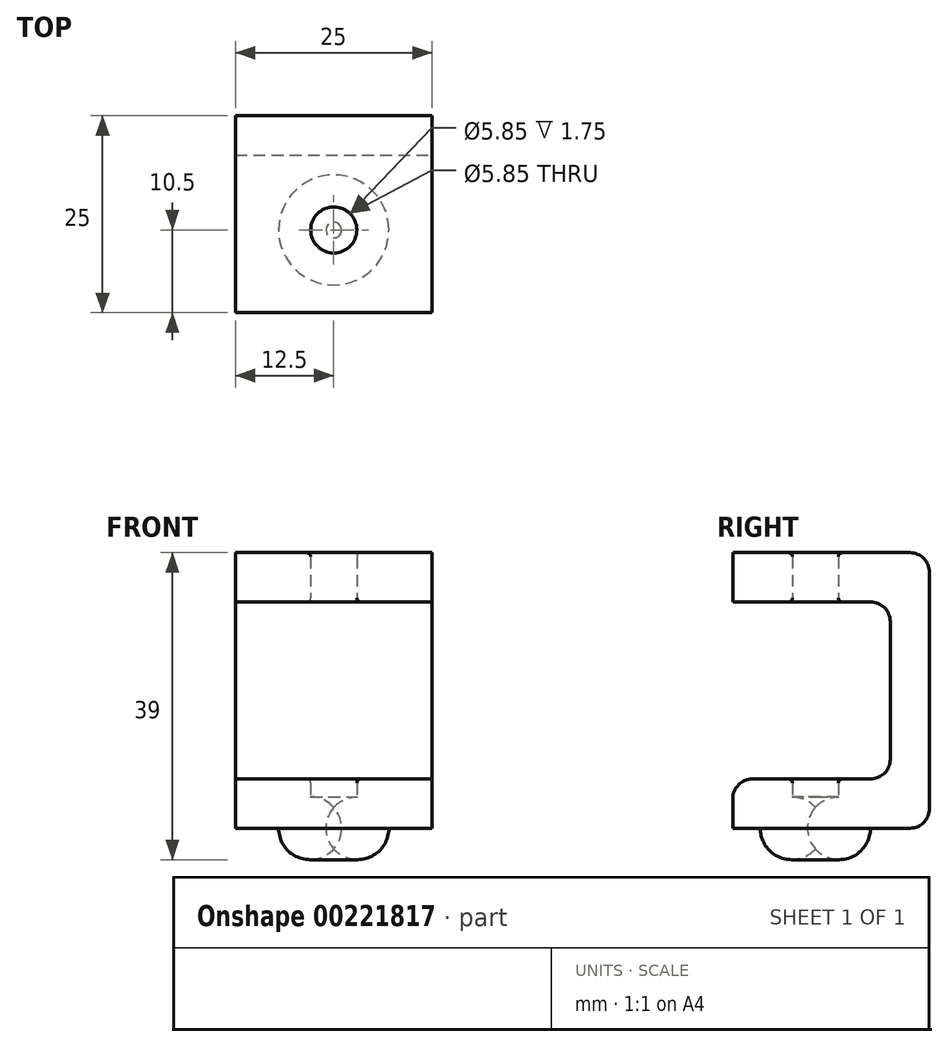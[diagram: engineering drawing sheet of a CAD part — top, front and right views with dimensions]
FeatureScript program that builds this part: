
annotation { "Feature Type Name" : "Feature", "Feature Type Description" : "" }
export const myFeature = defineFeature(function(context is Context, id is Id, definition is map)
    precondition{}
    {
        {
            var Q0;
            Q0=qCreatedBy(makeId("Top.planeOp"),FACE);
            var sketch = newSketch(context, id + "F0", { "sketchPlane" : qUnion([Q0])});
            skLineSegment(sketch, "E0.bottom", {"start": v(-12.5, -12.5) * mm, "end": v(12.5, -12.5) * mm});
            skLineSegment(sketch, "E0.top", {"start": v(-12.5, 12.5) * mm, "end": v(12.5, 12.5) * mm});
            skLineSegment(sketch, "E0.left", {"start": v(-12.5, -12.5) * mm, "end": v(-12.5, 12.5) * mm});
            skLineSegment(sketch, "E0.right", {"start": v(12.5, -12.5) * mm, "end": v(12.5, 12.5) * mm});
            skPoint(sketch, "E0.middle", {"position": v(0, 0) * mm});
            skLineSegment(sketch, "E1", {"start": v(0, -12.5) * mm, "end": v(0, 0) * mm, "construction": true});
            skCircle(sketch, "E2", {"center": v(0, -2) * mm, "radius": 2.93 * mm});
            skCircle(sketch, "E3", {"center": v(0, -2) * mm, "radius": 7 * mm});
            skSolve(sketch);
        }
        {
            var Q0;
            Q0=makeQuery(id+"F0.imprint","IMPRINT",FACE,{"disambiguationData":[TD([[makeQuery(id+"F0.imprint","IMPRINT",EDGE,{"derivedFrom":sQuery(id+"F0.wireOp",EDGE,"E0.bottom")}),1.0]])]});
            var Q1;
            Q1=makeQuery(id+"F0.imprint","IMPRINT",FACE,{"disambiguationData":[TD([[makeQuery(id+"F0.imprint","IMPRINT",EDGE,{"derivedFrom":sQuery(id+"F0.wireOp",EDGE,"E2")}),-1.0]])]});
            var Q2;
            Q2=makeQuery(id+"F0.imprint","IMPRINT",FACE,{"disambiguationData":[TD([[makeQuery(id+"F0.imprint","IMPRINT",EDGE,{"derivedFrom":sQuery(id+"F0.wireOp",EDGE,"E2")}),1.0]])]});
            extrude(context, id + "F1", {"entities" : qUnion([Q0, Q1, Q2]), "depth" : 35 * mm, "offsetDistance" : 25 * mm});
        }
        {
            var Q0;
            Q0=makeQuery(id+"F1.opExtrude","SWEPT_FACE",FACE,{"disambiguationData":[OSD([sQuery(id+"F0.wireOp",EDGE,"E0.bottom")])]});
            var sketch = newSketch(context, id + "F2", { "sketchPlane" : qUnion([Q0])});
            skLineSegment(sketch, "E4.bottom", {"start": v(-12.5, 6.25) * mm, "end": v(12.5, 6.25) * mm});
            skLineSegment(sketch, "E4.top", {"start": v(-12.5, 28.75) * mm, "end": v(12.5, 28.75) * mm});
            skLineSegment(sketch, "E4.left", {"start": v(-12.5, 6.25) * mm, "end": v(-12.5, 28.75) * mm});
            skLineSegment(sketch, "E4.right", {"start": v(12.5, 6.25) * mm, "end": v(12.5, 28.75) * mm});
            skPoint(sketch, "E4.middle", {"position": v(0, 17.5) * mm});
            skPoint(sketch, "E4.middle.positionSnap0", {"position": v(-12.5, 17.5) * mm});
            skPoint(sketch, "E4.centerSnap0", {"position": v(-12.5, 17.5) * mm});
            skSolve(sketch);
        }
        {
            var Q0;
            Q0 = qSketchRegion(id + "F2", true);
            extrude(context, id + "F3", {"entities" : qUnion([Q0]), "operationType" : NewBodyOperationType.REMOVE, "oppositeDirection" : true, "depth" : 20 * mm, "offsetDistance" : 25 * mm});
        }
        {
            var Q0;
            Q0=makeQuery(id+"F0.imprint","IMPRINT",FACE,{"disambiguationData":[TD([[makeQuery(id+"F0.imprint","IMPRINT",EDGE,{"derivedFrom":sQuery(id+"F0.wireOp",EDGE,"E2")}),1.0]])]});
            var Q1;
            Q1=makeQuery(id+"F1.opExtrude","SWEPT_BODY",BODY,{"disambiguationData":[OSD([sQuery(id+"F0.wireOp",EDGE,"E0.bottom"),sQuery(id+"F0.wireOp",EDGE,"E0.top"),sQuery(id+"F0.wireOp",EDGE,"E0.left"),sQuery(id+"F0.wireOp",EDGE,"E0.right")])]});
            extrude(context, id + "F4", {"entities" : qUnion([Q0]), "operationType" : NewBodyOperationType.REMOVE, "endBound" : BoundingType.THROUGH_ALL, "depth" : 25 * mm, "endBoundEntityBody" : qUnion([Q1]), "offsetDistance" : 25 * mm});
        }
        {
            var Q0;
            Q0=makeQuery(id+"F1.opExtrude","CAP_FACE",FACE,{"disambiguationData":[OSD([sQuery(id+"F0.wireOp",EDGE,"E0.bottom"),sQuery(id+"F0.wireOp",EDGE,"E0.top"),sQuery(id+"F0.wireOp",EDGE,"E0.left"),sQuery(id+"F0.wireOp",EDGE,"E0.right")])],"isStart":true});
            var sketch = newSketch(context, id + "F5", { "sketchPlane" : qUnion([Q0])});
            skCircle(sketch, "E5.0", {"center": v(0, 2) * mm, "radius": 7 * mm});
            skSolve(sketch);
        }
        {
            var Q0;
            Q0 = qSketchRegion(id + "F5", true);
            extrude(context, id + "F6", {"entities" : qUnion([Q0]), "operationType" : NewBodyOperationType.REMOVE, "oppositeDirection" : true, "depth" : 4 * mm, "offsetDistance" : 25 * mm});
        }
        {
            var Q0;
            Q0=makeQuery(id+"F3.boolean.opBoolean","COPY",EDGE,{"derivedFrom":makeQuery(id+"F3.opExtrude","CAP_EDGE",EDGE,{"disambiguationData":[OSD([sQuery(id+"F2.wireOp",EDGE,"E4.bottom")])],"isStart":false})});
            var Q1;
            Q1=makeQuery(id+"F3.boolean.opBoolean","COPY",EDGE,{"derivedFrom":makeQuery(id+"F3.opExtrude","CAP_EDGE",EDGE,{"disambiguationData":[OSD([sQuery(id+"F2.wireOp",EDGE,"E4.top")])],"isStart":false})});
            var Q2;
            Q2=makeQuery(id+"F1.opExtrude","CAP_EDGE",EDGE,{"disambiguationData":[OSD([sQuery(id+"F0.wireOp",EDGE,"E0.top")])],"isStart":false});
            var Q3;
            Q3=makeQuery(id+"F1.opExtrude","CAP_EDGE",EDGE,{"disambiguationData":[OSD([sQuery(id+"F0.wireOp",EDGE,"E0.top")])],"isStart":true});
            var Q4;
            Q4=makeQuery(id+"F3.boolean.opBoolean","COPY",EDGE,{"derivedFrom":makeQuery(id+"F3.opExtrude","CAP_EDGE",EDGE,{"disambiguationData":[OSD([sQuery(id+"F2.wireOp",EDGE,"E4.top")])],"isStart":true})});
            var Q5;
            Q5=makeQuery(id+"F3.boolean.opBoolean","COPY",EDGE,{"derivedFrom":makeQuery(id+"F3.opExtrude","CAP_EDGE",EDGE,{"disambiguationData":[OSD([sQuery(id+"F2.wireOp",EDGE,"E4.bottom")])],"isStart":true})});
            fillet(context, id + "F7", {"entities" : qUnion([Q0, Q1, Q2, Q3, Q4, Q5]), "tangentPropagation" : true, "radius" : 2.5 * mm, "defaultsChanged" : false, "vertexSettings" : [], "allowEdgeOverflow" : false});
        }
        {
            var Q0;
            Q0=makeQuery(id+"F6.boolean.opBoolean","COPY",EDGE,{"derivedFrom":makeQuery(id+"F6.opExtrude","CAP_EDGE",EDGE,{"disambiguationData":[OSD([sQuery(id+"F5.wireOp",EDGE,"E5.0")])],"isStart":false})});
            fillet(context, id + "F8", {"entities" : qUnion([Q0]), "tangentPropagation" : true, "radius" : 4 * mm, "defaultsChanged" : true, "vertexSettings" : [], "allowEdgeOverflow" : false});
        }
        {
            var Q0;
            Q0=makeQuery(id+"F4.boolean.opBoolean","INTERSECT",EDGE,{"derivedFrom":[makeQuery(id+"F1.opExtrude","CAP_FACE",FACE,{"disambiguationData":[OSD([sQuery(id+"F0.wireOp",EDGE,"E0.bottom"),sQuery(id+"F0.wireOp",EDGE,"E0.top"),sQuery(id+"F0.wireOp",EDGE,"E0.left"),sQuery(id+"F0.wireOp",EDGE,"E0.right")])],"isStart":false}),makeQuery(id+"F4.opExtrude","SWEPT_FACE",FACE,{"disambiguationData":[OSD([sQuery(id+"F0.wireOp",EDGE,"E2")])]})]});
            var Q1;
            Q1=makeQuery(id+"F4.boolean.opBoolean","INTERSECT",EDGE,{"derivedFrom":[makeQuery(id+"F3.boolean.opBoolean","COPY",FACE,{"derivedFrom":makeQuery(id+"F3.opExtrude","SWEPT_FACE",FACE,{"disambiguationData":[OSD([sQuery(id+"F2.wireOp",EDGE,"E4.top")])]})}),makeQuery(id+"F4.opExtrude","SWEPT_FACE",FACE,{"disambiguationData":[OSD([sQuery(id+"F0.wireOp",EDGE,"E2")])]})]});
            var Q2;
            Q2=makeQuery(id+"F8.opFillet","BLEND_EDGE",EDGE,{"blendedFrom":[makeQuery(id+"F6.boolean.opBoolean","COPY",EDGE,{"derivedFrom":makeQuery(id+"F6.opExtrude","CAP_EDGE",EDGE,{"disambiguationData":[OSD([sQuery(id+"F5.wireOp",EDGE,"E5.0")])],"isStart":false})}),makeQuery(id+"F4.boolean.opBoolean","COPY",FACE,{"disambiguationData":[TD([makeQuery(id+"F3.boolean.opBoolean","COPY",FACE,{"derivedFrom":makeQuery(id+"F3.opExtrude","SWEPT_FACE",FACE,{"disambiguationData":[OSD([sQuery(id+"F2.wireOp",EDGE,"E4.bottom")])]})})])],"derivedFrom":makeQuery(id+"F4.opExtrude","SWEPT_FACE",FACE,{"disambiguationData":[OSD([sQuery(id+"F0.wireOp",EDGE,"E2")])]})})],"blendedInto":[makeQuery(id+"F4.boolean.opBoolean","COPY",FACE,{"disambiguationData":[TD([makeQuery(id+"F3.boolean.opBoolean","COPY",FACE,{"derivedFrom":makeQuery(id+"F3.opExtrude","SWEPT_FACE",FACE,{"disambiguationData":[OSD([sQuery(id+"F2.wireOp",EDGE,"E4.bottom")])]})})])],"derivedFrom":makeQuery(id+"F4.opExtrude","SWEPT_FACE",FACE,{"disambiguationData":[OSD([sQuery(id+"F0.wireOp",EDGE,"E2")])]})})]});
            var Q3;
            Q3=makeQuery(id+"F4.boolean.opBoolean","INTERSECT",EDGE,{"derivedFrom":[makeQuery(id+"F3.boolean.opBoolean","COPY",FACE,{"derivedFrom":makeQuery(id+"F3.opExtrude","SWEPT_FACE",FACE,{"disambiguationData":[OSD([sQuery(id+"F2.wireOp",EDGE,"E4.bottom")])]})}),makeQuery(id+"F4.opExtrude","SWEPT_FACE",FACE,{"disambiguationData":[OSD([sQuery(id+"F0.wireOp",EDGE,"E2")])]})]});
            fillet(context, id + "F9", {"entities" : qUnion([Q0, Q1, Q2, Q3]), "tangentPropagation" : true, "radius" : .5 * mm, "defaultsChanged" : false, "vertexSettings" : [], "allowEdgeOverflow" : false});
        }
    });
